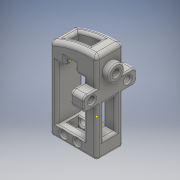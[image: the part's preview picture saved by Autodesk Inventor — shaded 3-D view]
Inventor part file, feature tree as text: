
AUTODESK INVENTOR PART (.ipt)
format: ipt  version: 2016 (Build 200138000, 138)  size: 627,712 bytes
history: native  units: mm
features: fillet x29, sketch x11, extrude x9
ambient origin geometry x8: Origin, YZ Plane, XZ Plane, XY Plane, X Axis, Y Axis, Z Axis, Center Point
bodies: Solid1 (feature_tree)
feature tree (49):
  extrude  "MainChassis"  Depth=9.0mm
  extrude  "wireSlot"  Depth=2.0mm TaperAngle=0.0deg
  fillet  "Fillet2"  [1 undecoded]
  fillet  "Fillet3"  Radius=7.0mm
  fillet  "Fillet4"  Radius=6.0mm
  fillet  "Fillet5"  Radius=5.0mm
  fillet  "Fillet6"  Radius=10.0mm
  fillet  "Fillet8"  Radius=2.0mm
  fillet  "Fillet9"  Radius=2.0mm
  fillet  "Fillet11"  Radius=2.0mm
  fillet  "Fillet13"  Radius=2.0mm
  fillet  "Fillet14"  Radius=2.0mm
  fillet  "Fillet16"  Radius=2.0mm
  fillet  "Fillet18"  Radius=2.0mm
  sketch  "Sketch3"  dims[d26=2.0mm d27=2.0mm]
  fillet  "Fillet19"  Radius=2.0mm
  extrude  "ServoScrewHoles"  Depth=2.0mm
  extrude  "horn"  Depth=2.0mm
  extrude  "innerHorn"  Depth=3.69mm
  sketch  "Sketch6"  dims[d38=12.0mm d39=2.0mm]
  extrude  "wings"  Depth=2.0mm
  extrude  "wingScrewHoles"  TaperAngle=0.0deg  [1 undecoded]
  fillet  "Fillet30"  Radius=12.0mm
  fillet  "Fillet31"  Radius=8.0mm
  fillet  "Fillet32"  Radius=5.0mm
  fillet  "Fillet34"  Radius=4.0mm
  fillet  "Fillet35"  Radius=4.9mm
  fillet  "Fillet36"  Radius=3.55mm
  extrude  "topGap"  Depth=12.0mm
  fillet  "Fillet39"  Radius=12.0mm
  sketch  "Sketch10"  dims[d87=1.0mm]
  extrude  "lateralHole"  Depth=10.0mm TaperAngle=0.0deg
  fillet  "Fillet40"  Radius=4.9mm
  fillet  "Fillet41"  Radius=13.5mm
  fillet  "Fillet42"  Radius=13.5mm
  fillet  "Fillet43"  Radius=4.9mm
  fillet  "Fillet44"  Radius=13.5mm
  fillet  "Fillet45"  Radius=13.5mm
  fillet  "Fillet46"  Radius=10.0mm
  fillet  "Fillet47"  Radius=40.5mm
  fillet  "Fillet48"  Radius=1.0mm
  sketch  "Sketch1"  dims[d0=20.0mm d2=9.0mm]
  sketch  "Sketch2"  dims[d3=10.0mm d4=20.0mm d5=0.0mm d6=0.0mm d7=7.0mm d9=6.0mm d11=5.0mm d12=10.0mm d13=0.0mm d15=2.0mm d16=2.0mm d17=2.0mm d18=2.0mm d19=2.0mm d21=2.0mm d22=2.0mm d24=2.0mm]
  sketch  "Sketch4"  dims[d29=2.0mm d31=2.0mm]
  sketch  "Sketch5"  dims[d35=4.9mm d36=3.69mm]
  sketch  "Sketch7"  dims[d40=10.17mm d41=0.0mm d42=0.0mm d50=12.0mm d52=8.0mm d53=5.0mm d54=0.0mm d55=4.0mm d56=0.0mm d58=4.9mm d59=3.55mm]
  sketch  "Sketch8"  dims[d60=22.0mm d61=0.0mm d63=12.0mm d64=12.0mm]
  sketch  "Sketch9"  dims[d65=11.0mm d66=10.0mm d67=0.0mm d74=4.9mm d75=13.5mm d76=13.5mm d77=4.9mm d78=13.5mm d79=13.5mm d80=10.0mm d81=0.0mm d85=40.5mm d86=1.0mm]
  sketch  "Sketch11"  dims[d88=3.0mm d90=1.0mm d91=1.0mm d93=4.0mm d94=8.1mm d95=1.0mm d99=11.4mm d100=10.0mm d101=2.0mm d102=5.5mm d103=5.5mm d104=10.0mm d105=0.0mm d106=10.0mm d107=180.0deg d108=3.189771mm d109=3.0mm d110=8.0mm d111=5.0mm d112=4.0mm d113=4.0mm d114=10.0mm d115=0.0mm d116=3.0mm d117=2.0mm d118=2.0mm d119=1.0mm d120=2.0mm d121=2.0mm d122=1.0mm d123=2.0mm d124=2.0mm]
note: 2 required parameter values undecoded (feature->parameter linkage not recoverable at this tier; creation-order binding heuristic only, values carry confidence <= 0.55)
